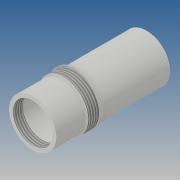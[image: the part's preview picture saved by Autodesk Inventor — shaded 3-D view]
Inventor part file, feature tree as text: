
AUTODESK INVENTOR PART (.ipt)
format: ipt  version: 2019 (Build 230136000, 136)  size: 131,584 bytes
history: native  units: mm
features: other x3, chamfer x1, sketch x1
ambient origin geometry x8: Origin, YZ Plane, XZ Plane, XY Plane, X Axis, Y Axis, Z Axis, Center Point
bodies: Body1 (feature_tree)
feature tree (5):
  other  "Révolution1"
  other  "Filetage2"
  chamfer  "Chanfrein4"  Distance=1.5mm
  other  "Filetage3"
  sketch  "Esquisse3"
